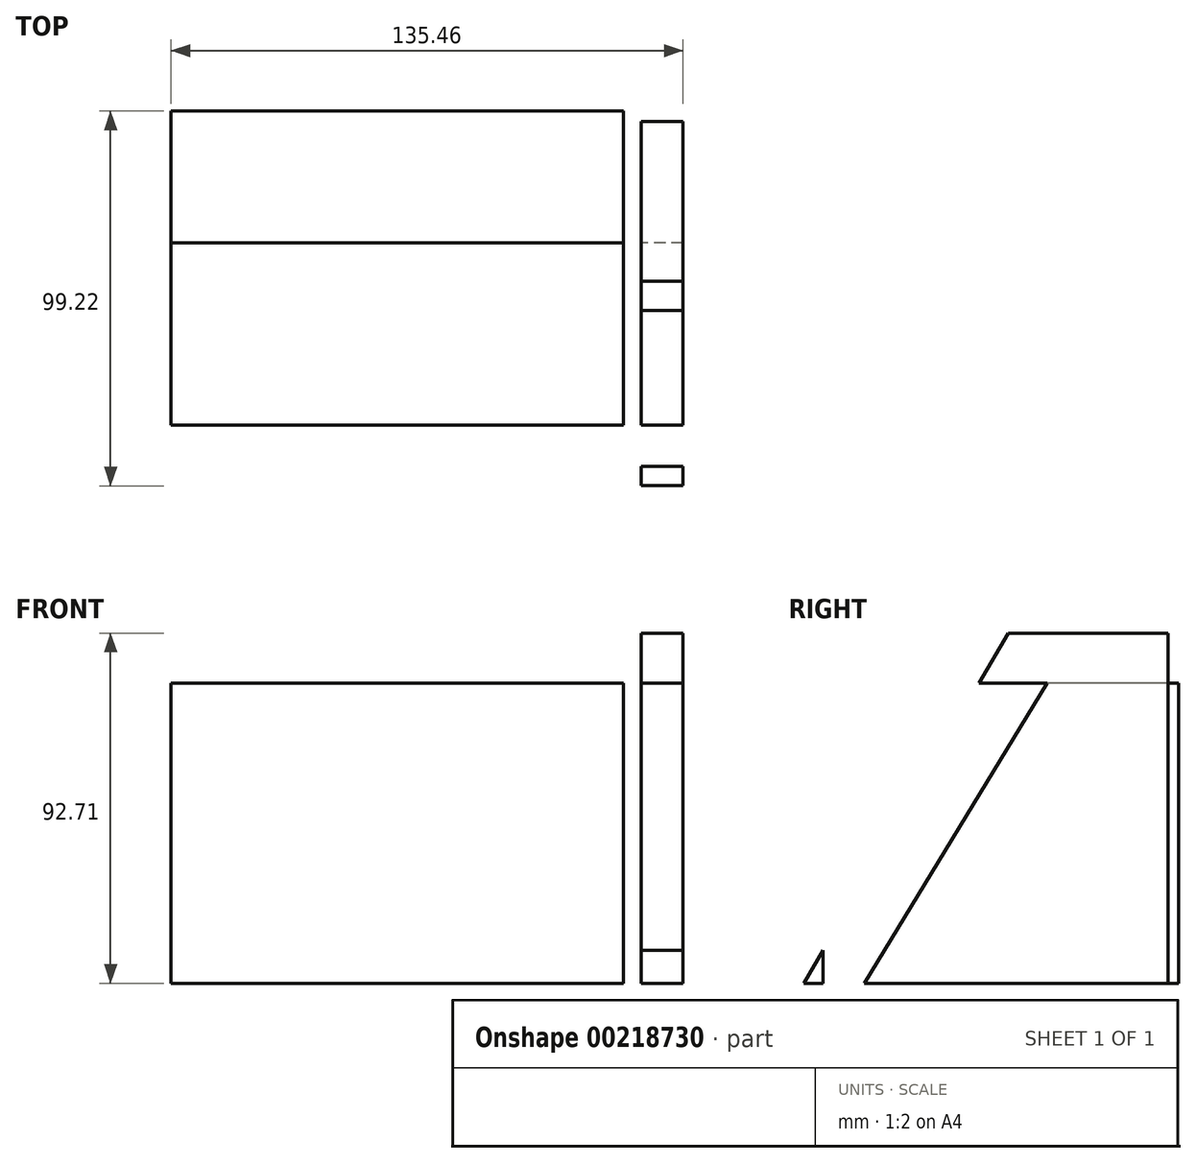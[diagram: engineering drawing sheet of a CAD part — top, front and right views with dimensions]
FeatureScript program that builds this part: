
annotation { "Feature Type Name" : "Feature", "Feature Type Description" : "" }
export const myFeature = defineFeature(function(context is Context, id is Id, definition is map)
    precondition{}
    {
        {
            var Q0;
            Q0=qCreatedBy(makeId("Top.planeOp"),FACE);
            var sketch = newSketch(context, id + "F0", { "sketchPlane" : qUnion([Q0])});
            skLineSegment(sketch, "E0.bottom", {"start": v(-61.51, 45.08) * mm, "end": v(58.15, 45.08) * mm});
            skLineSegment(sketch, "E0.top", {"start": v(-61.51, -49.01) * mm, "end": v(58.15, -49.01) * mm});
            skLineSegment(sketch, "E0.left", {"start": v(-61.51, 45.08) * mm, "end": v(-61.51, -49.01) * mm});
            skLineSegment(sketch, "E0.right", {"start": v(58.15, 45.08) * mm, "end": v(58.15, -49.01) * mm});
            skSolve(sketch);
        }
        {
            var Q0;
            Q0=makeQuery(id+"F0.imprint","IMPRINT",FACE,{"disambiguationData":[TD([[makeQuery(id+"F0.imprint","IMPRINT",EDGE,{"derivedFrom":sQuery(id+"F0.wireOp",EDGE,"E0.bottom")}),-1.0]])]});
            extrude(context, id + "F1", {"entities" : qUnion([Q0]), "depth" : 79.5 * mm});
        }
        {
            var Q0;
            Q0=qCreatedBy(makeId("Top.planeOp"),FACE);
            var sketch = newSketch(context, id + "F2", { "sketchPlane" : qUnion([Q0])});
            skLineSegment(sketch, "E1", {"start": v(62.86, 42.32) * mm, "end": v(73.95, 42.32) * mm});
            skLineSegment(sketch, "E2", {"start": v(62.86, 42.32) * mm, "end": v(62.86, -52.92) * mm});
            skLineSegment(sketch, "E3", {"start": v(62.86, -52.92) * mm, "end": v(62.86, -60.82) * mm});
            skLineSegment(sketch, "E4", {"start": v(73.95, 42.32) * mm, "end": v(73.95, -60.82) * mm});
            skLineSegment(sketch, "E5", {"start": v(62.86, -60.82) * mm, "end": v(73.95, -60.82) * mm});
            skSolve(sketch);
        }
        {
            var Q0;
            Q0=makeQuery(id+"F2.imprint","IMPRINT",FACE,{"disambiguationData":[TD([[makeQuery(id+"F2.imprint","IMPRINT",EDGE,{"derivedFrom":sQuery(id+"F2.wireOp",EDGE,"E1")}),-1.0]])]});
            extrude(context, id + "F3", {"entities" : qUnion([Q0]), "depth" : 92.7 * mm});
        }
        {
            var Q0;
            Q0=makeQuery(id+"F1.opExtrude","SWEPT_FACE",FACE,{"disambiguationData":[OSD([sQuery(id+"F0.wireOp",EDGE,"E0.left")])]});
            var sketch = newSketch(context, id + "F4", { "sketchPlane" : qUnion([Q0])});
            skLineSegment(sketch, "E6.0.0", {"start": v(-45.08, 0) * mm, "end": v(49.01, 0) * mm});
            skLineSegment(sketch, "E6.0.1", {"start": v(49.01, 0) * mm, "end": v(49.01, 79.5) * mm});
            skLineSegment(sketch, "E6.0.2", {"start": v(49.01, 79.5) * mm, "end": v(-45.08, 79.5) * mm});
            skLineSegment(sketch, "E6.0.3", {"start": v(-45.08, 79.5) * mm, "end": v(-45.08, 0) * mm});
            skLineSegment(sketch, "E7", {"start": v(-10.22, 79.5) * mm, "end": v(38.12, 0) * mm});
            skLineSegment(sketch, "E8", {"start": v(-10.22, 79.5) * mm, "end": v(49.01, 79.5) * mm});
            skLineSegment(sketch, "E9", {"start": v(49.01, 79.5) * mm, "end": v(49.01, 5.33) * mm});
            skLineSegment(sketch, "E10", {"start": v(49.01, 5.33) * mm, "end": v(49.01, 0) * mm});
            skLineSegment(sketch, "E11", {"start": v(38.12, 0) * mm, "end": v(49.01, 0) * mm});
            skSolve(sketch);
        }
        {
            var Q0;
            Q0=makeQuery(id+"F4.imprint","IMPRINT",FACE,{"disambiguationData":[TD([[makeQuery(id+"F4.imprint","IMPRINT",EDGE,{"derivedFrom":sQuery(id+"F4.wireOp",EDGE,"E7")}),1.0]])]});
            extrude(context, id + "F5", {"entities" : qUnion([Q0]), "operationType" : NewBodyOperationType.REMOVE, "endBound" : BoundingType.THROUGH_ALL, "oppositeDirection" : true, "depth" : 25.4 * mm});
        }
        {
            var Q0;
            Q0=makeQuery(id+"F3.opExtrude","SWEPT_FACE",FACE,{"disambiguationData":[OSD([sQuery(id+"F2.wireOp",EDGE,"E2"),sQuery(id+"F2.wireOp",EDGE,"E3")])]});
            var sketch = newSketch(context, id + "F6", { "sketchPlane" : qUnion([Q0])});
            skLineSegment(sketch, "E12.0.0", {"start": v(-42.32, 0) * mm, "end": v(60.82, 0) * mm});
            skLineSegment(sketch, "E12.0.1", {"start": v(60.82, 0) * mm, "end": v(60.82, 92.7) * mm});
            skLineSegment(sketch, "E12.0.2", {"start": v(60.82, 92.7) * mm, "end": v(-42.32, 92.7) * mm});
            skLineSegment(sketch, "E12.0.3", {"start": v(-42.32, 92.7) * mm, "end": v(-42.32, 0) * mm});
            skLineSegment(sketch, "E13", {"start": v(0, 92.7) * mm, "end": v(54.14, 0) * mm});
            skLineSegment(sketch, "E14", {"start": v(0, 92.7) * mm, "end": v(60.82, 92.7) * mm});
            skLineSegment(sketch, "E15", {"start": v(60.82, 92.7) * mm, "end": v(60.82, 0) * mm});
            skLineSegment(sketch, "E16", {"start": v(60.82, 0) * mm, "end": v(54.14, 0) * mm});
            skSolve(sketch);
        }
        {
            var Q0;
            Q0=makeQuery(id+"F6.imprint","IMPRINT",FACE,{"disambiguationData":[TD([[makeQuery(id+"F6.imprint","IMPRINT",EDGE,{"derivedFrom":sQuery(id+"F6.wireOp",EDGE,"E13")}),1.0]])]});
            extrude(context, id + "F7", {"entities" : qUnion([Q0]), "operationType" : NewBodyOperationType.REMOVE, "endBound" : BoundingType.THROUGH_ALL, "oppositeDirection" : true, "depth" : 25.4 * mm});
        }
    });
